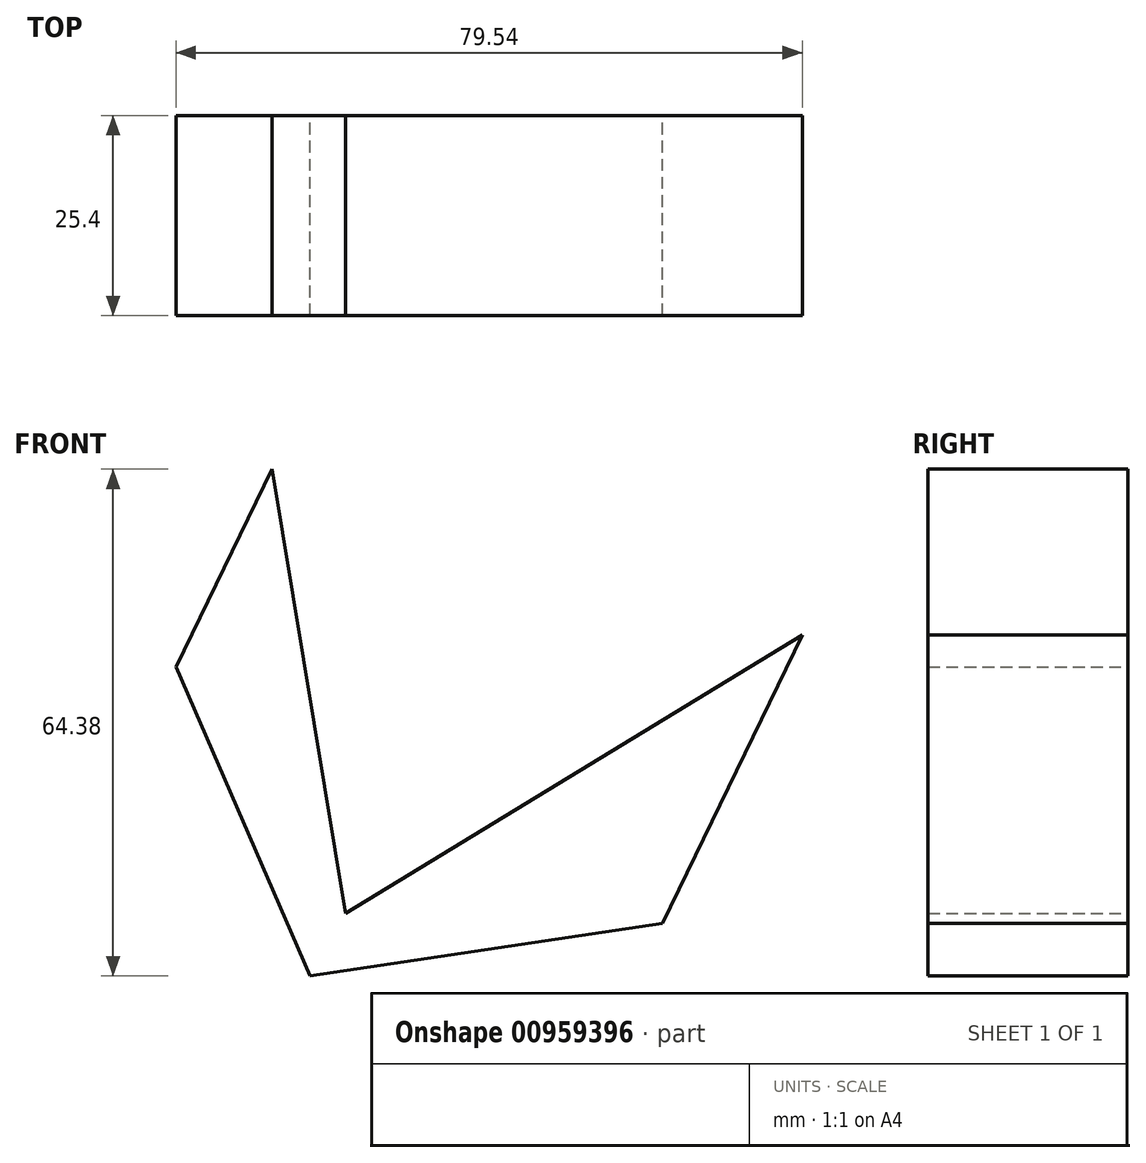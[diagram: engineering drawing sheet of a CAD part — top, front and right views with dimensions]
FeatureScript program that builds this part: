
annotation { "Feature Type Name" : "Feature", "Feature Type Description" : "" }
export const myFeature = defineFeature(function(context is Context, id is Id, definition is map)
    precondition{}
    {
        {
            var Q0;
            Q0=qCreatedBy(makeId("Front.planeOp"),FACE);
            var sketch = newSketch(context, id + "F0", { "sketchPlane" : qUnion([Q0])});
            skLineSegment(sketch, "E0", {"start": v(-42.45, 15.63) * mm, "end": v(-30.24, 40.79) * mm});
            skLineSegment(sketch, "E1", {"start": v(-30.24, 40.79) * mm, "end": v(-20.91, -15.68) * mm});
            skLineSegment(sketch, "E2", {"start": v(-20.91, -15.68) * mm, "end": v(37.09, 19.7) * mm});
            skLineSegment(sketch, "E3", {"start": v(37.09, 19.7) * mm, "end": v(19.33, -16.93) * mm});
            skLineSegment(sketch, "E4", {"start": v(19.33, -16.93) * mm, "end": v(-25.44, -23.59) * mm});
            skLineSegment(sketch, "E5", {"start": v(-25.44, -23.59) * mm, "end": v(-42.45, 15.63) * mm});
            skSolve(sketch);
        }
        {
            var Q0;
            Q0=qSketchRegion(id+"F0",true);
            extrude(context, id + "F1", {"entities" : qUnion([Q0]), "depth" : 25.4 * mm, "offsetDistance" : 25.4 * mm});
        }
    });
